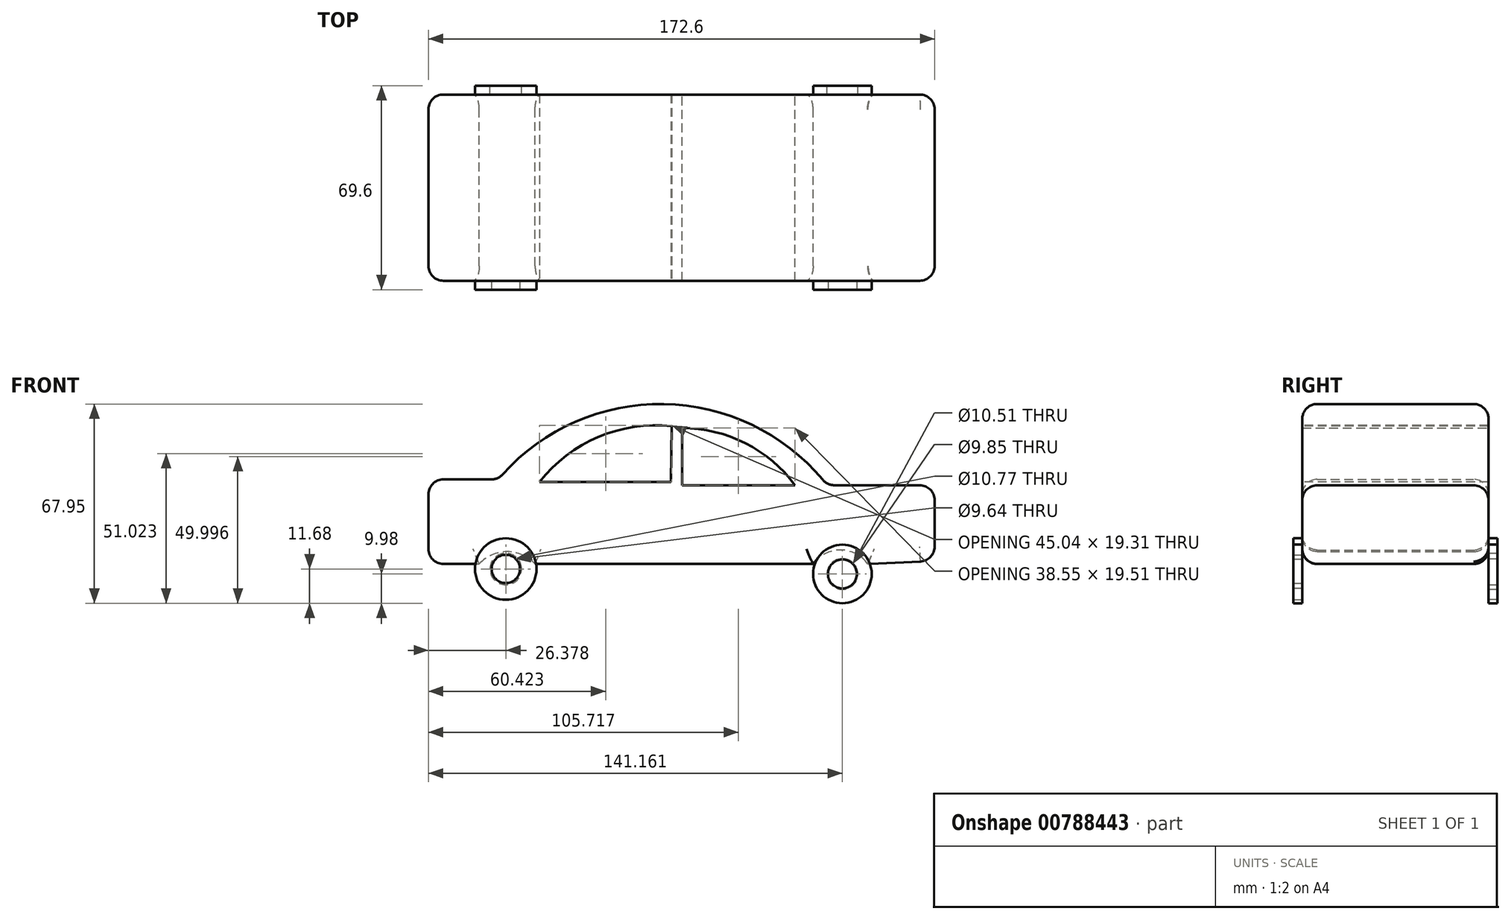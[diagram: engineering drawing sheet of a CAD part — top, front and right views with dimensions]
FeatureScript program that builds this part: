
annotation { "Feature Type Name" : "Feature", "Feature Type Description" : "" }
export const myFeature = defineFeature(function(context is Context, id is Id, definition is map)
    precondition{}
    {
        {
            var Q0;
            Q0=qCreatedBy(makeId("Front.planeOp"),FACE);
            var sketch = newSketch(context, id + "F0", { "sketchPlane" : qUnion([Q0])});
            skArc(sketch, "E0", {"start": v(49.52, 21.12) * mm, "mid": v(-6.1, 48.8) * mm, "end": v(-62.67, 23.08) * mm});
            skLineSegment(sketch, "E1", {"start": v(-62.67, 23.08) * mm, "end": v(-86.44, 23.08) * mm});
            skLineSegment(sketch, "E2", {"start": v(-86.44, 23.08) * mm, "end": v(-86.44, -5.73) * mm});
            skLineSegment(sketch, "E3", {"start": v(-86.44, -5.73) * mm, "end": v(-69.1, -5.73) * mm});
            skArc(sketch, "E4", {"start": v(-50.08, -5.73) * mm, "mid": v(-59.59, -1.54) * mm, "end": v(-69.1, -5.73) * mm});
            skLineSegment(sketch, "E5", {"start": v(-50.08, -5.73) * mm, "end": v(44.76, -5.73) * mm});
            skLineSegment(sketch, "E6", {"start": v(49.52, 21.12) * mm, "end": v(86.16, 21.12) * mm});
            skArc(sketch, "E7", {"start": v(63.36, -5.73) * mm, "mid": v(54.06, -0.97) * mm, "end": v(44.76, -5.73) * mm});
            skPoint(sketch, "E8.end.orphan", {"position": v(86.16, -4.67) * mm});
            skPoint(sketch, "E9.end.orphan", {"position": v(86.16, -5.73) * mm});
            skLineSegment(sketch, "E10", {"start": v(86.16, 21.12) * mm, "end": v(86.16, -4.67) * mm});
            skLineSegment(sketch, "E11", {"start": v(86.16, -4.67) * mm, "end": v(63.36, -5.73) * mm});
            skSolve(sketch);
        }
        {
            var Q0;
            Q0 = qSketchRegion(id + "F0", true);
            extrude(context, id + "F1", {"entities" : qUnion([Q0]), "endBound" : BoundingType.SYMMETRIC, "depth" : 63.5 * mm, "offsetDistance" : 25.4 * mm});
        }
        {
            var Q0;
            Q0=makeQuery(id+"F1.opExtrude","SWEPT_FACE",FACE,{"disambiguationData":[OSD([sQuery(id+"F0.wireOp",EDGE,"E6")])]});
            fillet(context, id + "F2", {"entities" : qUnion([Q0]), "radius" : 5.08 * mm, "tangentPropagation" : true, "allowEdgeOverflow" : false});
        }
        {
            var Q0;
            Q0=makeQuery(id+"F1.opExtrude","SWEPT_FACE",FACE,{"disambiguationData":[OSD([sQuery(id+"F0.wireOp",EDGE,"E1")])]});
            fillet(context, id + "F3", {"entities" : qUnion([Q0]), "radius" : 5.08 * mm, "tangentPropagation" : true, "allowEdgeOverflow" : false});
        }
        {
            var Q0;
            Q0=makeQuery(id+"F1.opExtrude","CAP_FACE",FACE,{"disambiguationData":[OSD([sQuery(id+"F0.wireOp",EDGE,"E0"),sQuery(id+"F0.wireOp",EDGE,"E1"),sQuery(id+"F0.wireOp",EDGE,"E2"),sQuery(id+"F0.wireOp",EDGE,"E3"),sQuery(id+"F0.wireOp",EDGE,"E4"),sQuery(id+"F0.wireOp",EDGE,"E5"),sQuery(id+"F0.wireOp",EDGE,"E6"),sQuery(id+"F0.wireOp",EDGE,"E7"),sQuery(id+"F0.wireOp",EDGE,"E10"),sQuery(id+"F0.wireOp",EDGE,"E11")])],"isStart":true});
            fillet(context, id + "F4", {"entities" : qUnion([Q0]), "radius" : 5.08 * mm, "tangentPropagation" : true, "allowEdgeOverflow" : false});
        }
        {
            var Q0;
            Q0=makeQuery(id+"F1.opExtrude","CAP_FACE",FACE,{"disambiguationData":[OSD([sQuery(id+"F0.wireOp",EDGE,"E0"),sQuery(id+"F0.wireOp",EDGE,"E1"),sQuery(id+"F0.wireOp",EDGE,"E2"),sQuery(id+"F0.wireOp",EDGE,"E3"),sQuery(id+"F0.wireOp",EDGE,"E4"),sQuery(id+"F0.wireOp",EDGE,"E5"),sQuery(id+"F0.wireOp",EDGE,"E6"),sQuery(id+"F0.wireOp",EDGE,"E7"),sQuery(id+"F0.wireOp",EDGE,"E10"),sQuery(id+"F0.wireOp",EDGE,"E11")])],"isStart":false});
            var Q1;
            Q1=makeQuery(id+"F1.opExtrude","SWEPT_FACE",FACE,{"disambiguationData":[OSD([sQuery(id+"F0.wireOp",EDGE,"E10")])]});
            fillet(context, id + "F5", {"entities" : qUnion([Q0, Q1]), "radius" : 5.08 * mm, "tangentPropagation" : true, "allowEdgeOverflow" : false});
        }
        {
            var Q0;
            Q0=makeQuery(id+"F1.opExtrude","SWEPT_FACE",FACE,{"disambiguationData":[OSD([sQuery(id+"F0.wireOp",EDGE,"E2")])]});
            fillet(context, id + "F6", {"entities" : qUnion([Q0]), "radius" : 5.08 * mm, "tangentPropagation" : true, "allowEdgeOverflow" : false});
        }
        {
            var Q0;
            Q0=makeQuery(id+"F1.opExtrude","CAP_FACE",FACE,{"disambiguationData":[OSD([sQuery(id+"F0.wireOp",EDGE,"E0"),sQuery(id+"F0.wireOp",EDGE,"E1"),sQuery(id+"F0.wireOp",EDGE,"E2"),sQuery(id+"F0.wireOp",EDGE,"E3"),sQuery(id+"F0.wireOp",EDGE,"E4"),sQuery(id+"F0.wireOp",EDGE,"E5"),sQuery(id+"F0.wireOp",EDGE,"E6"),sQuery(id+"F0.wireOp",EDGE,"E7"),sQuery(id+"F0.wireOp",EDGE,"E10"),sQuery(id+"F0.wireOp",EDGE,"E11")])],"isStart":true});
            var sketch = newSketch(context, id + "F7", { "sketchPlane" : qUnion([Q0])});
            skArc(sketch, "E12", {"start": v(0, 40.62) * mm, "mid": v(-21.6, 35.46) * mm, "end": v(-38.55, 21.11) * mm});
            skLineSegment(sketch, "E13", {"start": v(-38.55, 21.11) * mm, "end": v(0, 21.11) * mm});
            skLineSegment(sketch, "E14", {"start": v(0, 40.62) * mm, "end": v(0, 21.11) * mm});
            skSolve(sketch);
        }
        {
            var Q0;
            Q0=makeQuery(id+"F7.imprint","IMPRINT",FACE,{"disambiguationData":[TD([[makeQuery(id+"F7.imprint","IMPRINT",EDGE,{"derivedFrom":sQuery(id+"F7.wireOp",EDGE,"E12")}),1.0]])]});
            extrude(context, id + "F8", {"entities" : qUnion([Q0]), "operationType" : NewBodyOperationType.REMOVE, "oppositeDirection" : true, "depth" : 100.84 * mm, "offsetDistance" : 25.4 * mm});
        }
        {
            var Q0;
            Q0=makeQuery(id+"F1.opExtrude","CAP_FACE",FACE,{"disambiguationData":[OSD([sQuery(id+"F0.wireOp",EDGE,"E0"),sQuery(id+"F0.wireOp",EDGE,"E1"),sQuery(id+"F0.wireOp",EDGE,"E2"),sQuery(id+"F0.wireOp",EDGE,"E3"),sQuery(id+"F0.wireOp",EDGE,"E4"),sQuery(id+"F0.wireOp",EDGE,"E5"),sQuery(id+"F0.wireOp",EDGE,"E6"),sQuery(id+"F0.wireOp",EDGE,"E7"),sQuery(id+"F0.wireOp",EDGE,"E10"),sQuery(id+"F0.wireOp",EDGE,"E11")])],"isStart":false});
            var sketch = newSketch(context, id + "F9", { "sketchPlane" : qUnion([Q0])});
            skArc(sketch, "E15", {"start": v(-3.5, 41.26) * mm, "mid": v(-28.48, 37.6) * mm, "end": v(-48.54, 22.24) * mm});
            skLineSegment(sketch, "E16", {"start": v(-48.54, 22.24) * mm, "end": v(-3.78, 22.24) * mm});
            skLineSegment(sketch, "E17", {"start": v(-3.78, 22.24) * mm, "end": v(-3.5, 41.26) * mm});
            skSolve(sketch);
        }
        {
            var Q0;
            Q0=makeQuery(id+"F9.imprint","IMPRINT",FACE,{"disambiguationData":[TD([[makeQuery(id+"F9.imprint","IMPRINT",EDGE,{"derivedFrom":sQuery(id+"F9.wireOp",EDGE,"E15")}),1.0]])]});
            extrude(context, id + "F10", {"entities" : qUnion([Q0]), "operationType" : NewBodyOperationType.REMOVE, "oppositeDirection" : true, "depth" : 87.88 * mm, "offsetDistance" : 25.4 * mm});
        }
        {
            var Q0;
            Q0=makeQuery(id+"F1.opExtrude","CAP_FACE",FACE,{"disambiguationData":[OSD([sQuery(id+"F0.wireOp",EDGE,"E0"),sQuery(id+"F0.wireOp",EDGE,"E1"),sQuery(id+"F0.wireOp",EDGE,"E2"),sQuery(id+"F0.wireOp",EDGE,"E3"),sQuery(id+"F0.wireOp",EDGE,"E4"),sQuery(id+"F0.wireOp",EDGE,"E5"),sQuery(id+"F0.wireOp",EDGE,"E6"),sQuery(id+"F0.wireOp",EDGE,"E7"),sQuery(id+"F0.wireOp",EDGE,"E10"),sQuery(id+"F0.wireOp",EDGE,"E11")])],"isStart":false});
            var sketch = newSketch(context, id + "F11", { "sketchPlane" : qUnion([Q0])});
            skCircle(sketch, "E18", {"center": v(-60.06, -7.45) * mm, "radius": 10.49 * mm});
            skCircle(sketch, "E19", {"center": v(54.72, -9.15) * mm, "radius": 9.98 * mm});
            skSolve(sketch);
        }
        {
            var Q0;
            Q0 = qSketchRegion(id + "F11", true);
            extrude(context, id + "F12", {"entities" : qUnion([Q0]), "depth" : 3.05 * mm, "offsetDistance" : 25.4 * mm});
        }
        {
            var Q0;
            Q0=makeQuery(id+"F12.opExtrude","SWEPT_BODY",BODY,{"disambiguationData":[OSD([sQuery(id+"F11.wireOp",EDGE,"E18")])]});
            var Q1;
            Q1=makeQuery(id+"F12.opExtrude","SWEPT_BODY",BODY,{"disambiguationData":[OSD([sQuery(id+"F11.wireOp",EDGE,"E19")])]});
            var Q2;
            Q2=qCreatedBy(makeId("Front.planeOp"),FACE);
            mirror(context, id + "F13", {"entities" : qUnion([Q0, Q1]), "mirrorPlane" : qUnion([Q2])});
        }
        {
            var Q0;
            Q0=makeQuery(id+"F13.opPattern","COPY",FACE,{"derivedFrom":makeQuery(id+"F12.opExtrude","CAP_FACE",FACE,{"disambiguationData":[OSD([sQuery(id+"F11.wireOp",EDGE,"E19")])],"isStart":false}),"instanceName":"1"});
            var sketch = newSketch(context, id + "F14", { "sketchPlane" : qUnion([Q0])});
            skCircle(sketch, "E20", {"center": v(-54.72, -9.15) * mm, "radius": 5.26 * mm});
            skSolve(sketch);
        }
        {
            var Q0;
            Q0 = qSketchRegion(id + "F14", true);
            extrude(context, id + "F15", {"entities" : qUnion([Q0]), "operationType" : NewBodyOperationType.REMOVE, "oppositeDirection" : true, "depth" : 25.4 * mm, "offsetDistance" : 25.4 * mm});
        }
        {
            var Q0;
            Q0=makeQuery(id+"F12.opExtrude","CAP_FACE",FACE,{"disambiguationData":[OSD([sQuery(id+"F11.wireOp",EDGE,"E19")])],"isStart":false});
            var sketch = newSketch(context, id + "F16", { "sketchPlane" : qUnion([Q0])});
            skCircle(sketch, "E21", {"center": v(54.72, -9.15) * mm, "radius": 4.93 * mm});
            skSolve(sketch);
        }
        {
            var Q0;
            Q0 = qSketchRegion(id + "F16", true);
            extrude(context, id + "F17", {"entities" : qUnion([Q0]), "operationType" : NewBodyOperationType.REMOVE, "oppositeDirection" : true, "depth" : 25.4 * mm, "offsetDistance" : 25.4 * mm});
        }
        {
            var Q0;
            Q0=makeQuery(id+"F13.opPattern","COPY",FACE,{"derivedFrom":makeQuery(id+"F12.opExtrude","CAP_FACE",FACE,{"disambiguationData":[OSD([sQuery(id+"F11.wireOp",EDGE,"E18")])],"isStart":false}),"instanceName":"1"});
            var sketch = newSketch(context, id + "F18", { "sketchPlane" : qUnion([Q0])});
            skCircle(sketch, "E22", {"center": v(60.06, -7.45) * mm, "radius": 5.39 * mm});
            skSolve(sketch);
        }
        {
            var Q0;
            Q0 = qSketchRegion(id + "F18", true);
            extrude(context, id + "F19", {"entities" : qUnion([Q0]), "operationType" : NewBodyOperationType.REMOVE, "oppositeDirection" : true, "depth" : 25.4 * mm, "offsetDistance" : 25.4 * mm});
        }
        {
            var Q0;
            Q0=makeQuery(id+"F12.opExtrude","CAP_FACE",FACE,{"disambiguationData":[OSD([sQuery(id+"F11.wireOp",EDGE,"E18")])],"isStart":true});
            var sketch = newSketch(context, id + "F20", { "sketchPlane" : qUnion([Q0])});
            skCircle(sketch, "E23", {"center": v(60.06, -7.45) * mm, "radius": 4.82 * mm});
            skSolve(sketch);
        }
        {
            var Q0;
            Q0 = qSketchRegion(id + "F20", true);
            extrude(context, id + "F21", {"entities" : qUnion([Q0]), "operationType" : NewBodyOperationType.REMOVE, "oppositeDirection" : true, "depth" : 25.4 * mm, "offsetDistance" : 25.4 * mm});
        }
        {
            var Q0;
            {var subQ0=sQuery(id+"F0.wireOp",EDGE,"E6");Q0=makeQuery(id+"F2.opFillet","BLEND_FACE",FACE,{"disambiguationData":[OSD([subQ0]),TDD([makeQuery(id+"F1.opExtrude","CAP_EDGE",EDGE,{"disambiguationData":[OSD([subQ0])],"isStart":true})])]});}
            var Q1;
            Q1=makeQuery(id+"F4.opFillet","BLEND_FACE",FACE,{"disambiguationData":[OSD([sQuery(id+"F0.wireOp",EDGE,"E10")])]});
            var Q2;
            Q2=makeQuery(id+"F4.opFillet","BLEND_FACE",FACE,{"disambiguationData":[OSD([sQuery(id+"F0.wireOp",EDGE,"E11")])]});
            fillet(context, id + "F22", {"entities" : qUnion([Q0, Q1, Q2]), "radius" : 0.2 * mm, "tangentPropagation" : true, "allowEdgeOverflow" : false});
        }
    });
